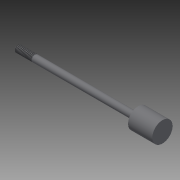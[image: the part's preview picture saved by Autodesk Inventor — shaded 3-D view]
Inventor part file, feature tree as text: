
AUTODESK INVENTOR PART (.ipt)
format: ipt  version: 2014 (Build 180170000, 170)  size: 125,440 bytes
history: native  units: in
note: dims shown in document units (in); Inventor stores cm internally (conversion verified against a paired STEP export)
features: other x49, revolve x3, sketch x3, thread x1
ambient origin geometry x8: Origin, YZ Plane, XZ Plane, XY Plane, X Axis, Y Axis, Z Axis, Center Point
bodies: Solid1 (feature_tree)
feature tree (56):
  revolve  "Revolution1"  [1 undecoded]
  thread  "Thread1"  [1 undecoded]
  revolve  "Revolution2"  [1 undecoded]
  revolve  "Revolution3"  [1 undecoded]
  other  "h1_XY"
  other  "h1_YZ"
  other  "h1_ZX"
  other  "h1_X"
  other  "h1_Y"
  other  "h1_Z"
  other  "h1_Center"
  other  "h2_XY"
  other  "h2_YZ"
  other  "h2_ZX"
  other  "h2_X"
  other  "h2_Y"
  other  "h2_Z"
  other  "h2_Center"
  other  "k1_XY"
  other  "k1_YZ"
  other  "k1_ZX"
  other  "k1_X"
  other  "k1_Y"
  other  "k1_Z"
  other  "k1_Center"
  other  "k2_XY"
  other  "k2_YZ"
  other  "k2_ZX"
  other  "k2_X"
  other  "k2_Y"
  other  "k2_Z"
  other  "k2_Center"
  other  "start_XY"
  other  "start_YZ"
  other  "start_ZX"
  other  "start_X"
  other  "start_Y"
  other  "start_Z"
  other  "start_Center"
  other  "to_prc_XY"
  other  "to_prc_YZ"
  other  "to_prc_ZX"
  other  "to_prc_X"
  other  "to_prc_Y"
  other  "to_prc_Z"
  other  "to_prc_Center"
  other  "to_rod_guide_XY"
  other  "to_rod_guide_YZ"
  other  "to_rod_guide_ZX"
  other  "to_rod_guide_X"
  other  "to_rod_guide_Y"
  other  "to_rod_guide_Z"
  other  "to_rod_guide_Center"
  sketch  "Sketch_3"  dims[d0=360.0deg d1=0.49in d2=3.541in d3=360.0deg]
  sketch  "Sketch_17"
  sketch  "Sketch_12"  dims[d4=360.0deg]
note: 4 required parameter values undecoded (feature->parameter linkage not recoverable at this tier; creation-order binding heuristic only, values carry confidence <= 0.55)